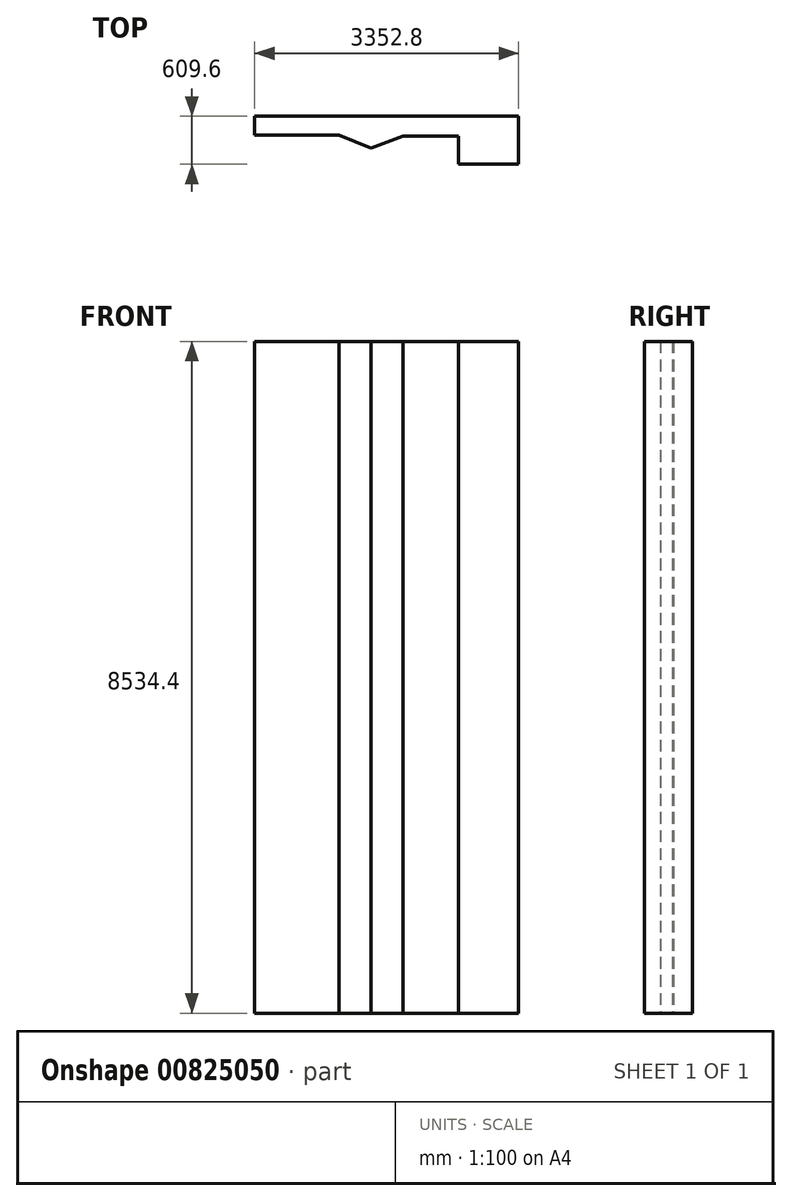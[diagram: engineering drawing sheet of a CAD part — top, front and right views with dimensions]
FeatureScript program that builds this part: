
annotation { "Feature Type Name" : "Feature", "Feature Type Description" : "" }
export const myFeature = defineFeature(function(context is Context, id is Id, definition is map)
    precondition{}
    {
        {
            var Q0;
            Q0=qCreatedBy(makeId("Top.planeOp"),FACE);
            var sketch = newSketch(context, id + "F0", { "sketchPlane" : qUnion([Q0])});
            skLineSegment(sketch, "E0", {"start": v(3352.8, 0) * mm, "end": v(0, 0) * mm});
            skLineSegment(sketch, "E1", {"start": v(0, 0) * mm, "end": v(0, -241.3) * mm});
            skLineSegment(sketch, "E2", {"start": v(0, -241.3) * mm, "end": v(1069.45, -241.3) * mm});
            skLineSegment(sketch, "E3", {"start": v(1475.85, -406.4) * mm, "end": v(1882.25, -254) * mm});
            skLineSegment(sketch, "E4", {"start": v(1882.25, -254) * mm, "end": v(2590.8, -254) * mm});
            skLineSegment(sketch, "E5", {"start": v(2590.8, -254) * mm, "end": v(2590.8, -609.6) * mm});
            skLineSegment(sketch, "E6", {"start": v(2590.8, -609.6) * mm, "end": v(3352.8, -609.6) * mm});
            skLineSegment(sketch, "E7", {"start": v(3352.8, -609.6) * mm, "end": v(3352.8, 0) * mm});
            skLineSegment(sketch, "E8", {"start": v(1475.85, -406.4) * mm, "end": v(1069.45, -241.3) * mm});
            skSolve(sketch);
        }
        {
            var Q0;
            Q0=makeQuery(id+"F0.imprint","IMPRINT",FACE,{"disambiguationData":[TD([[makeQuery(id+"F0.imprint","IMPRINT",EDGE,{"derivedFrom":sQuery(id+"F0.wireOp",EDGE,"E0")}),1.0]])]});
            extrude(context, id + "F1", {"entities" : qUnion([Q0]), "depth" : 8534.4 * mm, "offsetDistance" : 25.4 * mm});
        }
    });
